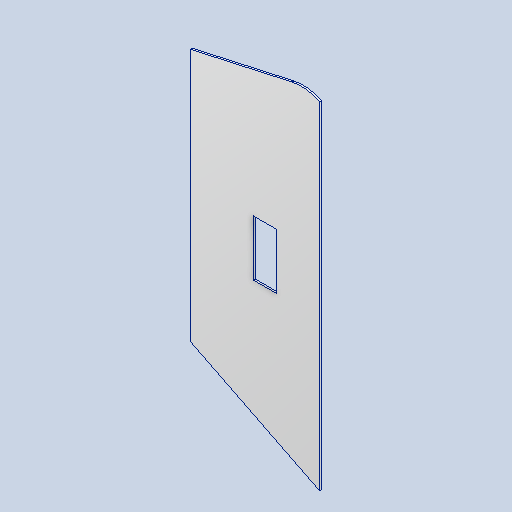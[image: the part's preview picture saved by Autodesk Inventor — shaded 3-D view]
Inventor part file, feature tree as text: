
AUTODESK INVENTOR PART (.ipt)
format: ipt  version: 2022.3 (Build 263350000, 350)  size: 131,584 bytes
history: native  units: mm
features: other x6, reference x5, extrude x2, sketch x2, projected_geometry x1
ambient origin geometry x8: Origin, YZ Plane, XZ Plane, XY Plane, X Axis, Y Axis, Z Axis, Center Point
bodies: Solid1 (feature_tree)
feature tree (16):
  extrude  "Extrusion1"  Depth=0.5mm TaperAngle=0.0deg
  extrude  "Extrusion2"  Depth=0.5mm
  sketch  "Sketch1"  dims[d0=0.5mm d1=0.0mm d2=0.5mm d3=0.0mm]
  reference  "Reference1"
  reference  "Reference2"
  reference  "Reference3"
  reference  "Reference4"
  reference  "Reference5"
  sketch  "Sketch2"  dims[d4=0.5mm d5=0.872665mm]
  projected_geometry  "Projected Loop1"
  other  "Assembly2"
  other  "sciana_lewa_v3:1"
  other  "pług:1"
  other  "pokrywa:1"
  other  "minisumopodsr:1"
  other  "koło_minisumo:1"
